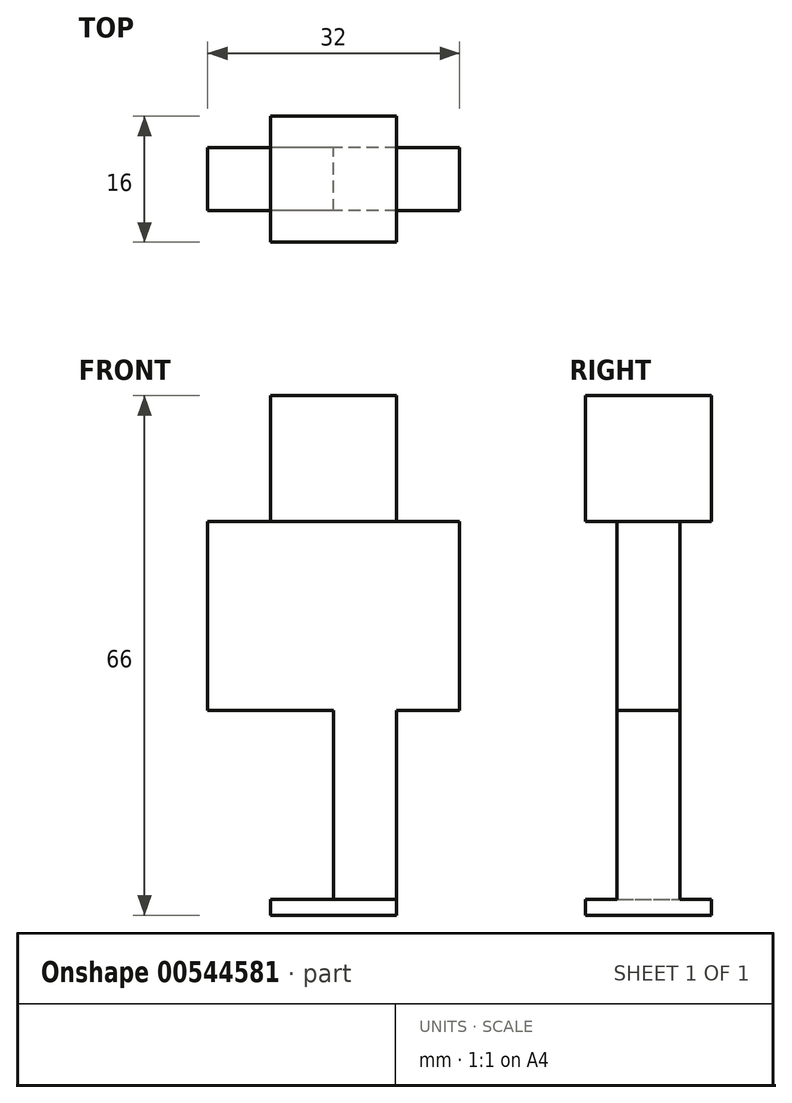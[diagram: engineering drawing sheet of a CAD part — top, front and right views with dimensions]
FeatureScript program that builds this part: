
annotation { "Feature Type Name" : "Feature", "Feature Type Description" : "" }
export const myFeature = defineFeature(function(context is Context, id is Id, definition is map)
    precondition{}
    {
        {
            var Q0;
            Q0=qCreatedBy(makeId("Front.planeOp"),FACE);
            var sketch = newSketch(context, id + "F0", { "sketchPlane" : qUnion([Q0])});
            skLineSegment(sketch, "E0.bottom", {"start": v(0, 19) * mm, "end": v(8, 19) * mm});
            skLineSegment(sketch, "E0.top", {"start": v(0, -5) * mm, "end": v(8, -5) * mm});
            skLineSegment(sketch, "E0.left", {"start": v(0, 19) * mm, "end": v(0, -5) * mm});
            skLineSegment(sketch, "E0.right", {"start": v(8, 19) * mm, "end": v(8, -5) * mm});
            skLineSegment(sketch, "E1.MirrorCS", {"start": v(0, -5) * mm, "end": v(-8, -5) * mm});
            skLineSegment(sketch, "E2.MirrorCS", {"start": v(-8, 19) * mm, "end": v(-8, -5) * mm});
            skLineSegment(sketch, "E3.MirrorCS", {"start": v(0, 19) * mm, "end": v(-8, 19) * mm});
            skLineSegment(sketch, "E4.bottom", {"start": v(-8, 19) * mm, "end": v(8, 19) * mm});
            skLineSegment(sketch, "E4.top", {"start": v(-8, 35) * mm, "end": v(8, 35) * mm});
            skLineSegment(sketch, "E4.left", {"start": v(-8, 19) * mm, "end": v(-8, 35) * mm});
            skLineSegment(sketch, "E4.right", {"start": v(8, 19) * mm, "end": v(8, 35) * mm});
            skLineSegment(sketch, "E5.bottom", {"start": v(-8, 19) * mm, "end": v(-16, 19) * mm});
            skLineSegment(sketch, "E5.top", {"start": v(-8, -5) * mm, "end": v(-16, -5) * mm});
            skLineSegment(sketch, "E5.right", {"start": v(-16, 19) * mm, "end": v(-16, -5) * mm});
            skLineSegment(sketch, "E6.MirrorCS", {"start": v(8, -5) * mm, "end": v(16, -5) * mm});
            skLineSegment(sketch, "E7.MirrorCS", {"start": v(16, 19) * mm, "end": v(16, -5) * mm});
            skLineSegment(sketch, "E8.MirrorCS", {"start": v(8, 19) * mm, "end": v(16, 19) * mm});
            skLineSegment(sketch, "E9.bottom", {"start": v(-8, -5) * mm, "end": v(0, -5) * mm});
            skLineSegment(sketch, "E9.top", {"start": v(-8, -29) * mm, "end": v(0, -29) * mm});
            skLineSegment(sketch, "E9.left", {"start": v(-8, -5) * mm, "end": v(-8, -29) * mm});
            skLineSegment(sketch, "E9.right", {"start": v(0, -5) * mm, "end": v(0, -29) * mm});
            skLineSegment(sketch, "E10.MirrorCS", {"start": v(8, -29) * mm, "end": v(0, -29) * mm});
            skLineSegment(sketch, "E11.MirrorCS", {"start": v(8, -5) * mm, "end": v(8, -29) * mm});
            skSolve(sketch);
        }
        {
            var Q0;
            {var subQ0=sQuery(id+"F0.wireOp",EDGE,"E0.left");Q0=makeQuery(id+"F0.imprint","IMPRINT",FACE,{"disambiguationData":[TD([[makeQuery(id+"F0.imprint","IMPRINT",EDGE,{"derivedFrom":subQ0}),-1.0]])]});}
            var Q1;
            Q1=makeQuery(id+"F0.imprint","IMPRINT",FACE,{"disambiguationData":[TD([[makeQuery(id+"F0.imprint","IMPRINT",EDGE,{"derivedFrom":sQuery(id+"F0.wireOp",EDGE,"E5.bottom")}),1.0]])]});
            var Q2;
            {var subQ0=sQuery(id+"F0.wireOp",EDGE,"E0.left");Q2=makeQuery(id+"F0.imprint","IMPRINT",FACE,{"disambiguationData":[TD([[makeQuery(id+"F0.imprint","IMPRINT",EDGE,{"derivedFrom":subQ0}),1.0]])]});}
            var Q3;
            Q3=makeQuery(id+"F0.imprint","IMPRINT",FACE,{"disambiguationData":[TD([[makeQuery(id+"F0.imprint","IMPRINT",EDGE,{"derivedFrom":sQuery(id+"F0.wireOp",EDGE,"E6.MirrorCS")}),1.0]])]});
            var Q4;
            Q4=makeQuery(id+"F0.imprint","IMPRINT",FACE,{"disambiguationData":[TD([[makeQuery(id+"F0.imprint","IMPRINT",EDGE,{"derivedFrom":sQuery(id+"F0.wireOp",EDGE,"E10.MirrorCS")}),-1.0]])]});
            var Q5;
            Q5=makeQuery(id+"F0.imprint","IMPRINT",FACE,{"disambiguationData":[TD([[makeQuery(id+"F0.imprint","IMPRINT",EDGE,{"derivedFrom":sQuery(id+"F0.wireOp",EDGE,"E9.bottom")}),-1.0]])]});
            var Q6;
            Q6=sQuery(id+"F0.wireOp",EDGE,"E5.right");
            var Q7;
            Q7=sQuery(id+"F0.wireOp",EDGE,"E5.bottom");
            var Q8;
            Q8=sQuery(id+"F0.wireOp",EDGE,"E4.bottom");
            var Q9;
            Q9=sQuery(id+"F0.wireOp",EDGE,"E8.MirrorCS");
            var Q10;
            Q10=sQuery(id+"F0.wireOp",EDGE,"E7.MirrorCS");
            var Q11;
            Q11=sQuery(id+"F0.wireOp",EDGE,"E6.MirrorCS");
            var Q12;
            Q12=sQuery(id+"F0.wireOp",EDGE,"E11.MirrorCS");
            var Q13;
            Q13=sQuery(id+"F0.wireOp",EDGE,"E10.MirrorCS");
            var Q14;
            Q14=sQuery(id+"F0.wireOp",EDGE,"E9.top");
            var Q15;
            Q15=sQuery(id+"F0.wireOp",EDGE,"E9.left");
            var Q16;
            Q16=sQuery(id+"F0.wireOp",EDGE,"E5.top");
            extrude(context, id + "F1", {"entities" : qUnion([Q0, Q1, Q2, Q3, Q4, Q5]), "surfaceEntities" : qUnion([Q6, Q7, Q8, Q9, Q10, Q11, Q12, Q13, Q14, Q15, Q16]), "endBound" : BoundingType.SYMMETRIC, "depth" : 8 * mm, "offsetDistance" : 25 * mm});
        }
        {
            var Q0;
            Q0=makeQuery(id+"F0.imprint","IMPRINT",FACE,{"disambiguationData":[TD([[makeQuery(id+"F0.imprint","IMPRINT",EDGE,{"derivedFrom":sQuery(id+"F0.wireOp",EDGE,"E4.top")}),-1.0]])]});
            extrude(context, id + "F2", {"entities" : qUnion([Q0]), "operationType" : NewBodyOperationType.ADD, "endBound" : BoundingType.SYMMETRIC, "depth" : 16 * mm, "offsetDistance" : 25 * mm});
        }
        {
            var Q0;
            Q0=makeQuery(id+"F1.opExtrude","SWEPT_FACE",FACE,{"disambiguationData":[OSD([sQuery(id+"F0.wireOp",EDGE,"E9.top"),sQuery(id+"F0.wireOp",EDGE,"E10.MirrorCS")])]});
            var sketch = newSketch(context, id + "F3", { "sketchPlane" : qUnion([Q0])});
            skLineSegment(sketch, "E12.bottom", {"start": v(-8, 8) * mm, "end": v(8, 8) * mm});
            skLineSegment(sketch, "E12.top", {"start": v(-8, -8) * mm, "end": v(8, -8) * mm});
            skLineSegment(sketch, "E12.left", {"start": v(-8, 8) * mm, "end": v(-8, -8) * mm});
            skLineSegment(sketch, "E12.right", {"start": v(8, 8) * mm, "end": v(8, -8) * mm});
            skSolve(sketch);
        }
        {
            var Q0;
            Q0 = qSketchRegion(id + "F3", true);
            extrude(context, id + "F4", {"entities" : qUnion([Q0]), "operationType" : NewBodyOperationType.ADD, "depth" : 2 * mm, "offsetDistance" : 25 * mm});
        }
    });
